# Revit family: agtatec_Record_RlvngDrsetSym_K41_CurtainWallPanel
name_source: partatom
category: Curtain Panels
revit_build: Autodesk Revit Architecture 2012 (Build: 20110916_2132(x64)
units: mm (PartAtom-declared; Revit-internal decimal feet)

## types (1)
- default
    AccessoryOptions = Contact manufacturer
    AlternativeDoorsetGlazing = Part of glazing spec
    AntiFingerTrapRequirement = Yes
    Assembly Code = B2030300
    BIMObjectName = agtatec_Record_RevolvingDoorsetSystem_K41_CurtainWallPanel
    BottomConstruction = agtatec_Record_Revolving Door, Stainless Steel
    CanopyCovering = agtatec_Record_Revolving Door, Sheet metal (Painted Steel)
    CanopyHeight = 570 mm  [stored 1.87008 ft]
    CanopyHeightOptions = 250 mm +
    CanopyRadius = 1300 mm  [stored 4.26509 ft]
    Capacity = <>
    Colour = Customer specific
    Configuration = 2, 3 or 4 leafs
    Construction Type = Automatic Revolving Door
    Cost = 0 $
    DepthOfRecessFloorFrame = 80 mm
    Description = 4-wing Revolving Door
    DiameterOptions = Internal 2000-4000 mm
    DoorIncluded = Yes
    DoorSeal = 1
    DoorWingOptions = 4 wings
    DoorsetFasteners = Screws
    DoorsetOperation = Automatic
    DoorsetOptions = Ridig, Sliding door, Display case
    DrumWallPanelFill = agtatec_Record_Revolving Door, Laminated Safety Glass (Clear)
    DurationUnit = year
    ElectronicLock = Yes
    ExternalDimensionOfFloorFrame = 2794 mm
    Finish = Powder coated, Anodized, customer specific
    FireExit = No
    Floor Frame (Ring) = Yes
    Flooring = agtatec_Record_Revolving Door, Felt Carpet
    FrameMaterial = Aluminium
    FrameProfile = Aluminium
    FrameSeal = Yes
    GlassLayers = 1
    GlassThickness1 = 0 mm  [stored 0 ft]
    GlassThickness2 = 0 mm  [stored 0 ft]
    GlassType = Part of glazing spec
    HandicapAccessible = No
    Handles = Yes
    HasDrive = Yes
    Height = 2770 mm  [stored 9.08793 ft]
    HeightOfFloorFrame = 65 mm  [stored 0.213255 ft]
    HeightUnderCanopyOptions = Passage height: 2000 - 3000 mm
    IfcExportAs = IfcDoorStyle
    IfcExportType = Door
    InnerRadius = 1271 mm  [stored 4.16995 ft]
    InsideDiameter = 2542 mm  [stored 8.3399 ft]
    IsExternal = Yes
    IssueDate = <>
    LeafColourOptions = All RAL, customer specific
    LeafPanelFill = agtatec_Record_Revolving Door, Laminated Safety Glass (Clear)
    LeafRotationAngle = 45.00°
    ManufacturerName = Record
    ManufacturerURL = www.agta-record.com
    Material = Aluminium
    Model = K41
    ModelReference = Depends on the configuration
    NBSDescription = Revolving Doorset System
    NBSReference = 25-50-20/170
    Name = RlvngDrsetSym_K41_CurtainWallPanel_Record
    NightShutterPanelFill = agtatec_Record_Revolving Door, Laminated Safety Glass (Clear)
    NightShuttersOpen = Yes
    NominalHeight = 2770 mm  [stored 9.08793 ft]
    NominalLength = 2600 mm  [stored 8.53018 ft]
    NominalWidth = 2600 mm  [stored 8.53018 ft]
    OffsetFromWallCenter = 0 mm  [stored 0 ft]
    OperatingTemperature = -15º to +50ºC
    OuterRadius = 1297 mm  [stored 4.25525 ft]
    OutsideDiameter = 2594 mm
    PanelFrames = agtatec_Record_Revolving Door, Aluminium
    PanelHeight = 2163 mm
    PanelWidth = 1216 mm
    PassageHeight = 2200 mm
    PassageWidth = 1170 mm
    ProductInformation = www.agta-record.com
    RecessWidth = 2700 mm
    ReferenceStandard = EN16005, EN16361, DIN 18650, etc.
    ReplacementCost = Depends on the configuration and door type
    SafetyDevices = Fully compliant with EN16005, Safety buffers, Presence sensors, etc.
    SelfClosing = Yes
    ServiceLifeDuration = 10-15 years
    Shape = Cylinder shaped
    Showcase visibility = No
    SmokeStop = No
    ThermalTransmittance = 0
    ThresholdRequired = Yes
    ThresholdStripping = No additional required, part of the doorset
    TotalDiameter = 2600 mm  [stored 8.53018 ft]
    TotalHeight = 2770 mm  [stored 9.08793 ft]
    URL = www.agta-record.com
    Uniclass2 = Ss_25_30_20_70
    Version = Version 1.0
    WarrantyDescription = Depends on country
    WarrantyDurationLabour = Depends on country
    WarrantyDurationParts = Depends on country
    WarrantyDurationUnit = Depends on country
    WarrantyGuarantorLabour = Local door manufacturer
    WarrantyGuarantorParts = Local door manufacturer
    Weight = Depends on configuration and size
    Width = 2600 mm  [stored 8.53018 ft]
    WithinStandardSizes = Yes

note: [stored X ft] marks values corroborated as IEEE doubles in the binary element streams (Revit-internal decimal feet)

## geometry (parser evidence)
native form markers: Blend x12, Sweep x13
no freeform markers — native parametric forms only
